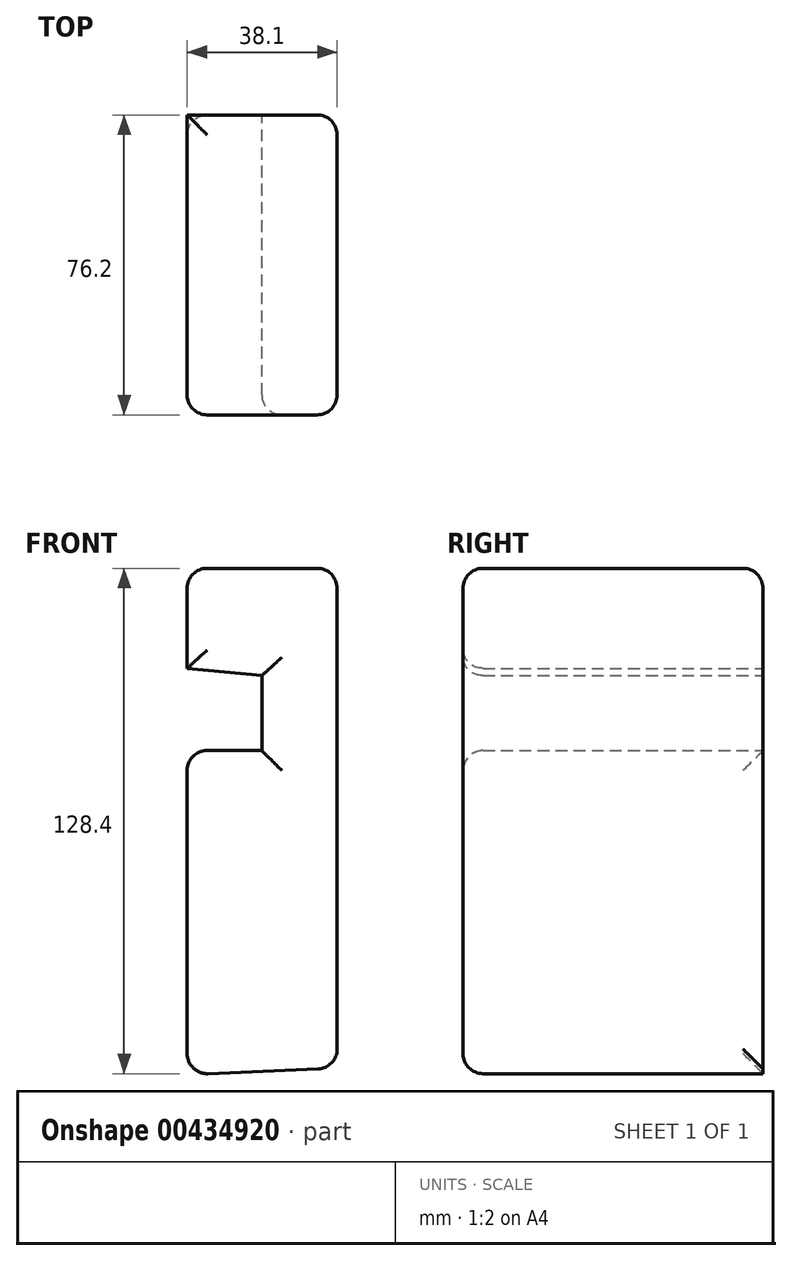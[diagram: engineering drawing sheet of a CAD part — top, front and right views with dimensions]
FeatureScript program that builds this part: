
annotation { "Feature Type Name" : "Feature", "Feature Type Description" : "" }
export const myFeature = defineFeature(function(context is Context, id is Id, definition is map)
    precondition{}
    {
        {
            var Q0;
            Q0=qCreatedBy(makeId("Front.planeOp"),FACE);
            var sketch = newSketch(context, id + "F0", { "sketchPlane" : qUnion([Q0])});
            skLineSegment(sketch, "E0", {"start": v(92.9, -74.85) * mm, "end": v(92.9, 52.15) * mm});
            skLineSegment(sketch, "E1", {"start": v(92.9, 52.15) * mm, "end": v(54.8, 52.15) * mm});
            skLineSegment(sketch, "E2", {"start": v(54.8, 52.15) * mm, "end": v(54.8, 26.75) * mm});
            skLineSegment(sketch, "E3", {"start": v(54.8, 26.75) * mm, "end": v(73.76, 24.9) * mm});
            skLineSegment(sketch, "E4", {"start": v(73.76, 24.9) * mm, "end": v(73.76, 5.84) * mm});
            skLineSegment(sketch, "E5", {"start": v(73.76, 5.84) * mm, "end": v(54.8, 5.84) * mm});
            skLineSegment(sketch, "E6", {"start": v(54.8, 5.84) * mm, "end": v(54.8, -76.47) * mm});
            skLineSegment(sketch, "E7", {"start": v(54.8, -76.47) * mm, "end": v(92.9, -74.85) * mm});
            skSolve(sketch);
        }
        {
            var Q0;
            Q0 = qSketchRegion(id + "F0", true);
            extrude(context, id + "F1", {"entities" : qUnion([Q0]), "depth" : 76.2 * mm});
        }
        {
            var Q0;
            Q0=makeQuery(id+"F1.opExtrude","CAP_EDGE",EDGE,{"disambiguationData":[OSD([sQuery(id+"F0.wireOp",EDGE,"E1")])],"isStart":false});
            var Q1;
            Q1=makeQuery(id+"F1.opExtrude","SWEPT_EDGE",EDGE,{"disambiguationData":[OSD([sQuery(id+"F0.wireOp",EDGE,"E1"),sQuery(id+"F0.wireOp",EDGE,"E2")])]});
            var Q2;
            Q2=makeQuery(id+"F1.opExtrude","CAP_FACE",FACE,{"disambiguationData":[OSD([sQuery(id+"F0.wireOp",EDGE,"E0"),sQuery(id+"F0.wireOp",EDGE,"E1"),sQuery(id+"F0.wireOp",EDGE,"E2"),sQuery(id+"F0.wireOp",EDGE,"E3"),sQuery(id+"F0.wireOp",EDGE,"E4"),sQuery(id+"F0.wireOp",EDGE,"E5"),sQuery(id+"F0.wireOp",EDGE,"E6"),sQuery(id+"F0.wireOp",EDGE,"E7")])],"isStart":false});
            var Q3;
            Q3=makeQuery(id+"F1.opExtrude","CAP_EDGE",EDGE,{"disambiguationData":[OSD([sQuery(id+"F0.wireOp",EDGE,"E6")])],"isStart":false});
            var Q4;
            Q4=makeQuery(id+"F1.opExtrude","SWEPT_FACE",FACE,{"disambiguationData":[OSD([sQuery(id+"F0.wireOp",EDGE,"E6")])]});
            var Q5;
            Q5=makeQuery(id+"F1.opExtrude","SWEPT_EDGE",EDGE,{"disambiguationData":[OSD([sQuery(id+"F0.wireOp",EDGE,"E0"),sQuery(id+"F0.wireOp",EDGE,"E1")])]});
            var Q6;
            Q6=makeQuery(id+"F1.opExtrude","CAP_EDGE",EDGE,{"disambiguationData":[OSD([sQuery(id+"F0.wireOp",EDGE,"E1")])],"isStart":true});
            var Q7;
            Q7=makeQuery(id+"F1.opExtrude","CAP_EDGE",EDGE,{"disambiguationData":[OSD([sQuery(id+"F0.wireOp",EDGE,"E0")])],"isStart":true});
            var Q8;
            Q8=makeQuery(id+"F1.opExtrude","CAP_EDGE",EDGE,{"disambiguationData":[OSD([sQuery(id+"F0.wireOp",EDGE,"E0")])],"isStart":false});
            var Q9;
            Q9=makeQuery(id+"F1.opExtrude","SWEPT_EDGE",EDGE,{"disambiguationData":[OSD([sQuery(id+"F0.wireOp",EDGE,"E0"),sQuery(id+"F0.wireOp",EDGE,"E7")])]});
            fillet(context, id + "F2", {"entities" : qUnion([Q0, Q1, Q2, Q3, Q4, Q5, Q6, Q7, Q8, Q9]), "radius" : 5.08 * mm, "tangentPropagation" : true, "allowEdgeOverflow" : false});
        }
    });
